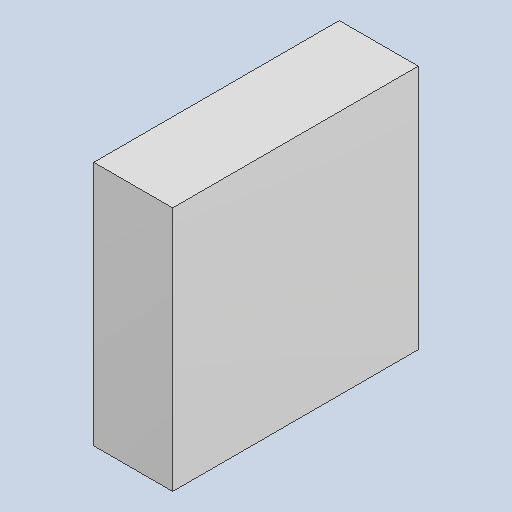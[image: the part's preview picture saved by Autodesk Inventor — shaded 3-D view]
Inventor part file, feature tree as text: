
AUTODESK INVENTOR PART (.ipt)
format: ipt  version: 2023.4 (Build 274418000, 418)  size: 81,408 bytes
history: native  units: mm
features: extrude x1
ambient origin geometry x8: Origin, YZ Plane, XZ Plane, XY Plane, X Axis, Y Axis, Z Axis, Center Point
bodies: Solid1 (feature_tree)
feature tree (1):
  extrude  "Extruded_11"  [1 undecoded]
note: 1 required parameter value undecoded (feature->parameter linkage not recoverable at this tier; creation-order binding heuristic only, values carry confidence <= 0.55)
